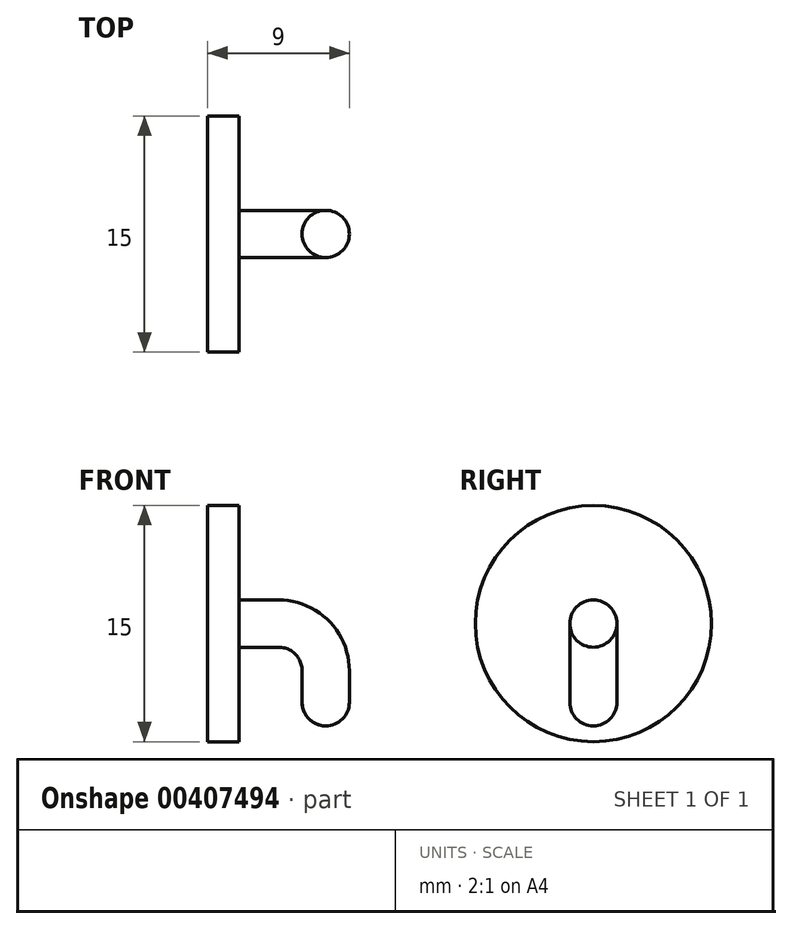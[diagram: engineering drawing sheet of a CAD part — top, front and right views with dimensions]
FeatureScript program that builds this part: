
annotation { "Feature Type Name" : "Feature", "Feature Type Description" : "" }
export const myFeature = defineFeature(function(context is Context, id is Id, definition is map)
    precondition{}
    {
        {
            var Q0;
            Q0=qCreatedBy(makeId("Right.planeOp"),FACE);
            var sketch = newSketch(context, id + "F0", { "sketchPlane" : qUnion([Q0])});
            skCircle(sketch, "E0", {"center": v(0, 0) * mm, "radius": 7.5 * mm});
            skSolve(sketch);
        }
        {
            var Q0;
            Q0=makeQuery(id+"F0.imprint","IMPRINT",FACE,{"disambiguationData":[TD([[makeQuery(id+"F0.imprint","IMPRINT",EDGE,{"derivedFrom":sQuery(id+"F0.wireOp",EDGE,"E0")}),1.0]])]});
            extrude(context, id + "F1", {"entities" : qUnion([Q0]), "oppositeDirection" : true, "depth" : 2 * mm, "offsetDistance" : 25.4 * mm});
        }
        {
            var Q0;
            Q0=qCreatedBy(makeId("Front.planeOp"),FACE);
            var sketch = newSketch(context, id + "F2", { "sketchPlane" : qUnion([Q0])});
            skLineSegment(sketch, "E1", {"start": v(0, 0) * mm, "end": v(2.5, 0) * mm});
            skLineSegment(sketch, "E2", {"start": v(5.5, -3) * mm, "end": v(5.5, -6.5) * mm});
            skPoint(sketch, "E3.visualSharp", {"position": v(5.5, 0) * mm});
            skArc(sketch, "E3.filletArc", {"start": v(5.5, -3) * mm, "mid": v(4.62, -0.88) * mm, "end": v(2.5, 0) * mm});
            skSolve(sketch);
        }
        {
            var Q0;
            Q0=qCreatedBy(makeId("Right.planeOp"),FACE);
            var sketch = newSketch(context, id + "F3", { "sketchPlane" : qUnion([Q0])});
            skCircle(sketch, "E4", {"center": v(0, 0) * mm, "radius": 1.5 * mm});
            skSolve(sketch);
        }
        {
            var Q0;
            Q0=makeQuery(id+"F3.imprint","IMPRINT",FACE,{"disambiguationData":[TD([[makeQuery(id+"F3.imprint","IMPRINT",EDGE,{"derivedFrom":sQuery(id+"F3.wireOp",EDGE,"E4")}),1.0]])]});
            var Q1;
            Q1=sQuery(id+"F2.wireOp",EDGE,"E1");
            var Q2;
            Q2=sQuery(id+"F2.wireOp",EDGE,"E3.filletArc");
            var Q3;
            Q3=sQuery(id+"F2.wireOp",EDGE,"E2");
            sweep(context, id + "F4", {"operationType" : NewBodyOperationType.ADD, "profiles" : qUnion([Q0]), "path" : qUnion([Q1, Q2, Q3])});
        }
        {
            var Q0;
            Q0=makeQuery(id+"F4.opSweep","CAP_EDGE",EDGE,{"disambiguationData":[OSD([sQuery(id+"F2.wireOp",VERTEX,"E2.end"),sQuery(id+"F3.wireOp",EDGE,"E4")])],"isStart":false});
            fillet(context, id + "F5", {"entities" : qUnion([Q0]), "radius" : 1.5 * mm, "tangentPropagation" : true, "allowEdgeOverflow" : false});
        }
    });
